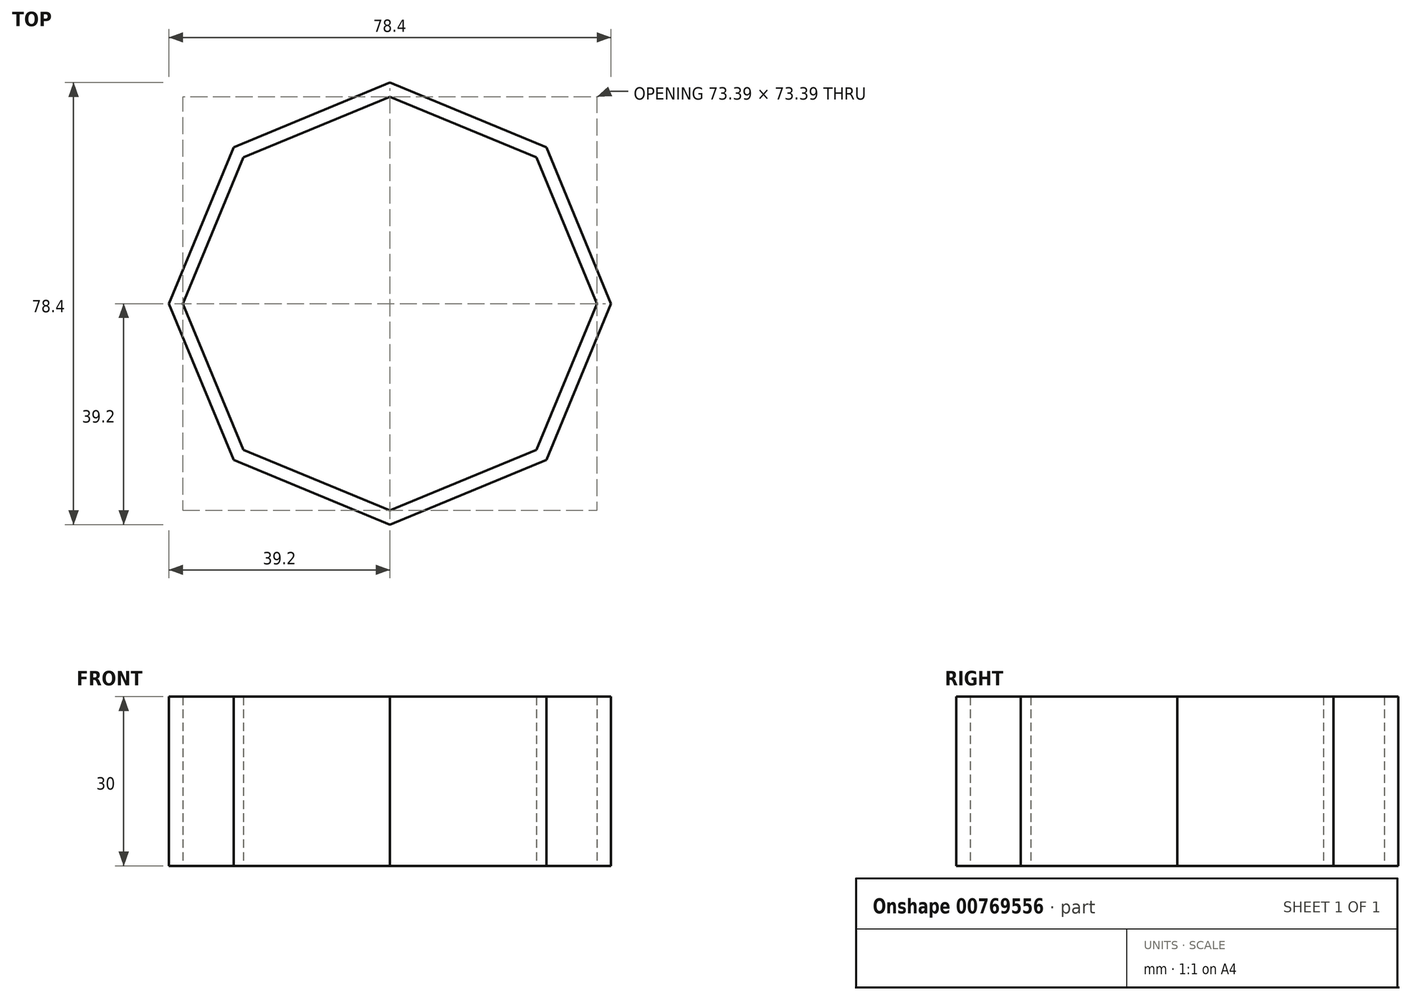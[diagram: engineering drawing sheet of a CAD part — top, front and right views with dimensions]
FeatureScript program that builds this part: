
annotation { "Feature Type Name" : "Feature", "Feature Type Description" : "" }
export const myFeature = defineFeature(function(context is Context, id is Id, definition is map)
    precondition{}
    {
        {
            var Q0;
            Q0=qCreatedBy(makeId("Top.planeOp"),FACE);
            var sketch = newSketch(context, id + "F0", { "sketchPlane" : qUnion([Q0])});
            skCircle(sketch, "E0.cCircle", {"center": v(0, 0) * mm, "radius": 39.2 * mm, "construction": true});
            skLineSegment(sketch, "E0.0", {"start": v(0, -39.2) * mm, "end": v(-27.72, -27.72) * mm});
            skLineSegment(sketch, "E0.1", {"start": v(-27.72, -27.72) * mm, "end": v(-39.2, 0) * mm});
            skLineSegment(sketch, "E0.2", {"start": v(-39.2, 0) * mm, "end": v(-27.72, 27.72) * mm});
            skLineSegment(sketch, "E0.3", {"start": v(-27.72, 27.72) * mm, "end": v(0, 39.2) * mm});
            skLineSegment(sketch, "E0.4", {"start": v(0, 39.2) * mm, "end": v(27.72, 27.72) * mm});
            skLineSegment(sketch, "E0.5", {"start": v(27.72, 27.72) * mm, "end": v(39.2, 0) * mm});
            skLineSegment(sketch, "E0.6", {"start": v(39.2, 0) * mm, "end": v(27.72, -27.72) * mm});
            skLineSegment(sketch, "E0.7", {"start": v(27.72, -27.72) * mm, "end": v(0, -39.2) * mm});
            skCircle(sketch, "E1.cCircle", {"center": v(0, 0) * mm, "radius": 36.7 * mm, "construction": true});
            skLineSegment(sketch, "E1.0", {"start": v(0, -36.7) * mm, "end": v(-25.95, -25.95) * mm});
            skLineSegment(sketch, "E1.1", {"start": v(-25.95, -25.95) * mm, "end": v(-36.7, 0) * mm});
            skLineSegment(sketch, "E1.2", {"start": v(-36.7, 0) * mm, "end": v(-25.95, 25.95) * mm});
            skLineSegment(sketch, "E1.3", {"start": v(-25.95, 25.95) * mm, "end": v(0, 36.7) * mm});
            skLineSegment(sketch, "E1.4", {"start": v(0, 36.7) * mm, "end": v(25.95, 25.95) * mm});
            skLineSegment(sketch, "E1.5", {"start": v(25.95, 25.95) * mm, "end": v(36.7, 0) * mm});
            skLineSegment(sketch, "E1.6", {"start": v(36.7, 0) * mm, "end": v(25.95, -25.95) * mm});
            skLineSegment(sketch, "E1.7", {"start": v(25.95, -25.95) * mm, "end": v(0, -36.7) * mm});
            skSolve(sketch);
        }
        {
            var Q0;
            Q0 = qSketchRegion(id + "F0", true);
            extrude(context, id + "F1", {"entities" : qUnion([Q0]), "depth" : 30 * mm, "offsetDistance" : 25 * mm});
        }
    });
